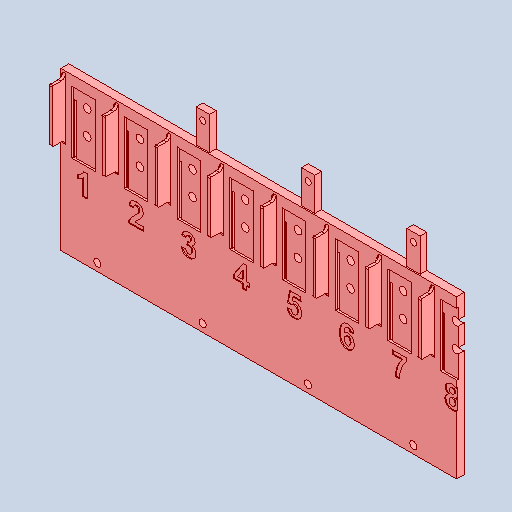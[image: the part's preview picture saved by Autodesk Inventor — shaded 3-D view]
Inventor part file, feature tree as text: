
AUTODESK INVENTOR PART (.ipt)
format: ipt  version: 2024.3 (Build 283343000, 343)  size: 1,187,328 bytes
history: native  units: in
note: dims shown in document units (in); Inventor stores cm internally (conversion verified against a paired STEP export)
features: sketch x19, extrude x10, other x5, hole x4, fillet x3, pattern_linear x1
ambient origin geometry x8: Origin, YZ Plane, XZ Plane, XY Plane, X Axis, Y Axis, Z Axis, Center Point
bodies: Solid1 (feature_tree)
feature tree (42):
  other  "main_manifold_8v_v02.ipt"
  other  "main_manifold_cover_1v_v02.ipt"
  other  "Honeywell3000.ipt"
  sketch  "Sketch:ref: assembly:XY"  dims[d204=0.0in]
  other  "x_Sketch:ref: assembly:YZ"
  sketch  "Sketch:MP:fSens header pins"  dims[d71=0.75in d72=0.375in d73=0.25in d74=0.5635in d75=0.25in d76=0.0in d133=0.18in]
  sketch  "Sketch:MP:fSens bottom groove"  dims[d136=0.75in d137=0.225in d138=0.25in d139=0.5635in d140=1.0in d141=0.8108in d148=0.018in]
  sketch  "Sketch:MP:fSens front wall"  dims[d168=0.029in d170=0.035in]
  sketch  "Sketch:MP: VH holes"  dims[d171=0.029in d203=0.0in]
  sketch  "Sketch:MP:base"  dims[d219=0.025in]
  sketch  "Sketch:MP: MM screws"  dims[d220=0.025in]
  sketch  "Sketch:MP:numbers_front"  dims[d222=0.1in]
  sketch  "Sketch:MP:numbers_back"  dims[d223=0.025in]
  extrude  "Ex: base"  Depth=0.2285in
  extrude  "Ex: fSens header pins"  TaperAngle=0.0deg  [1 undecoded]
  extrude  "Ex: fSens bottom groove"  Depth=0.18in
  extrude  "Ex: for PCB headers"  Depth=0.018in
  extrude  "Ex: fSens front wall"  Depth=0.035in
  hole  "Hole: fSens 4-40 thread insert"  [1 undecoded]
  pattern_linear  "Rectangular Pattern1"  Spacing1=2.4in  [1 undecoded]
  extrude  "Ex: extend top to MM screws"  Depth=2.4in
  extrude  "Ex: extend top cut flush to MM"  Depth=3.975in
  hole  "Hole: MM screws: 4-40 through hole"  [1 undecoded]
  extrude  "Ex: numbers: front"  Depth=0.175in
  extrude  "Ex: numbers: back"  Depth=9.0157in
  fillet  "Fillet1"  [1 undecoded]
  fillet  "Fillet2"  [1 undecoded]
  fillet  "Fillet4"  Radius=0.5in
  hole  "Hole: VH screws"  [1 undecoded]
  extrude  "cut to fit build plate"  Depth=0.5in
  hole  "Hole: for mounting PCB"  [1 undecoded]
  sketch  "Sketch:MM: main inlet"  dims[d244=0.02in]
  sketch  "Sketch:MM: prop valves"  dims[d245=0.0in]
  sketch  "Sketch:MM: prop valve cutout"  dims[d246=0.3in]
  sketch  "Sketch:MM: flow sensor"  dims[d247=0.5in]
  sketch  "Sketch:MM: MMC screws"  dims[d248=0.1in]
  sketch  "Sketch:MM: MP screws"  dims[d281=0.02in d282=0.0in]
  sketch  "Sketch:MM: mounting screws:1"  dims[d55=0.5in d64=0.2285in]
  sketch  "Sketch:MM: mounting screws:2"  dims[d65=0.2033in d57=0.0in]
  other  "MM front face"
  sketch  "Sketch:MMC: base"  dims[d285=0.165in d286=0.75in d287=0.225in d288=0.25in d289=0.5635in d290=1.0in d291=0.8108in]
  sketch  "Sketch:MP: PCB holes"  dims[d292=2.4in d293=2.4in d294=2.4in d295=3.975in d296=0.025in d297=0.175in d300=9.0157in d301=0.0in d302=0.0in d303=0.165in d304=0.75in d305=0.375in d306=0.25in d307=0.5635in d308=1.0in d309=0.8108in d145=0.5in d146=0.0344in d147=0.5in]
note: 8 required parameter values undecoded (feature->parameter linkage not recoverable at this tier; creation-order binding heuristic only, values carry confidence <= 0.55)
